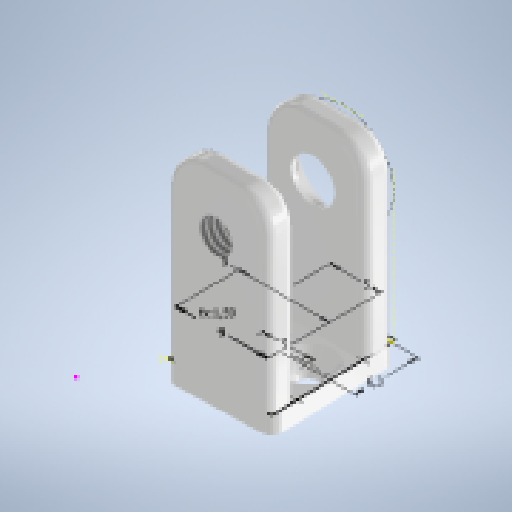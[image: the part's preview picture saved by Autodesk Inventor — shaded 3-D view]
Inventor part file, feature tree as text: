
AUTODESK INVENTOR PART (.ipt)
format: ipt  version: 2025 (Build 290162010, 162A)  size: 302,592 bytes
history: native  units: mm
features: sketch x3, hole x3, extrude x2, fillet x2
ambient origin geometry x8: Origin, YZ Plane, XZ Plane, XY Plane, X Axis, Y Axis, Z Axis, Center Point
bodies: Volumenkörper1 (feature_tree)
feature tree (10):
  extrude  "Extrusion1"  Depth=3.0mm
  fillet  "Rundung1"  Radius=3.0mm
  sketch  "Skizze2"  dims[d3=6.6mm d5=18.0mm d6=0.0mm]
  hole  "Bohrung1"  [1 undecoded]
  sketch  "Skizze4"  dims[d7=3.0mm d8=4.3mm d9=8.0mm d10=9.4mm d11=14.0mm d12=90.0deg d13=11.8mm d14=20.594885mm d19=2.0mm d20=8.0mm d21=5.0mm d22=2.0mm d23=90.0deg d24=8.0mm d25=20.594885mm d34=5.0mm d35=9.0mm d36=6.3mm d37=5.0mm d38=9.0mm d40=9.0mm d41=-0.277101mm d42=2.0mm d43=0.0mm d44=3.242mm d45=8.0mm d46=9.0mm d47=2.0mm d48=90.0deg d49=8.0mm d50=20.594885mm d51=1.0mm]
  extrude  "Extrusion3"  Depth=1.0mm
  hole  "Bohrung2"  [1 undecoded]
  hole  "Bohrung4"  [1 undecoded]
  fillet  "Rundung2"  Radius=5.0mm
  sketch  "Skizze1"  dims[d0=10.0mm d1=3.0mm d2=3.0mm]
note: 3 required parameter values undecoded (feature->parameter linkage not recoverable at this tier; creation-order binding heuristic only, values carry confidence <= 0.55)
